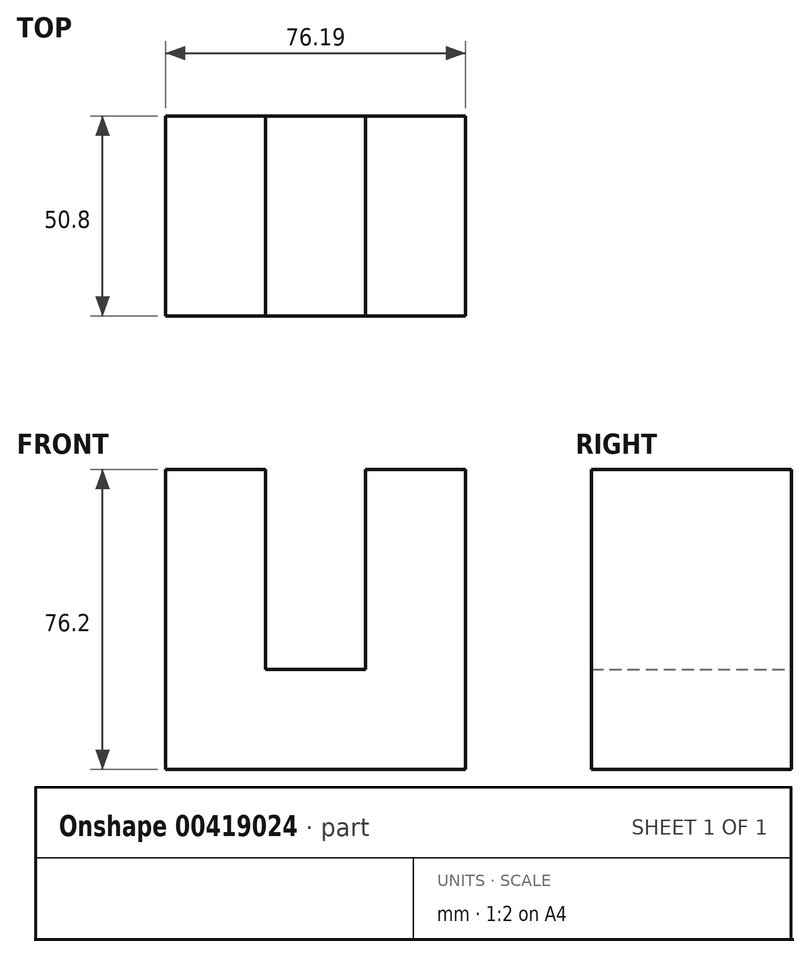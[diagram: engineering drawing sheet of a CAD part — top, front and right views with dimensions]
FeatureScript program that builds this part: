
annotation { "Feature Type Name" : "Feature", "Feature Type Description" : "" }
export const myFeature = defineFeature(function(context is Context, id is Id, definition is map)
    precondition{}
    {
        {
            var Q0;
            Q0=qCreatedBy(makeId("Front.planeOp"),FACE);
            var sketch = newSketch(context, id + "F0", { "sketchPlane" : qUnion([Q0])});
            skLineSegment(sketch, "E0", {"start": v(0, 0) * mm, "end": v(-76.2, 0) * mm});
            skLineSegment(sketch, "E1", {"start": v(-76.2, 0) * mm, "end": v(-76.2, 76.2) * mm});
            skLineSegment(sketch, "E2", {"start": v(-76.2, 76.2) * mm, "end": v(-50.78, 76.2) * mm});
            skLineSegment(sketch, "E3", {"start": v(-50.78, 76.2) * mm, "end": v(-50.78, 25.4) * mm});
            skLineSegment(sketch, "E4", {"start": v(0, 0) * mm, "end": v(0, 76.2) * mm});
            skLineSegment(sketch, "E5", {"start": v(0, 76.2) * mm, "end": v(-25.4, 76.2) * mm});
            skLineSegment(sketch, "E6", {"start": v(-25.4, 76.2) * mm, "end": v(-25.4, 25.4) * mm});
            skLineSegment(sketch, "E7", {"start": v(-25.4, 25.4) * mm, "end": v(-50.78, 25.4) * mm});
            skSolve(sketch);
        }
        {
            var Q0;
            Q0=makeQuery(id+"F0.imprint","IMPRINT",FACE,{"disambiguationData":[TD([[makeQuery(id+"F0.imprint","IMPRINT",EDGE,{"derivedFrom":sQuery(id+"F0.wireOp",EDGE,"E0")}),-1.0]])]});
            extrude(context, id + "F1", {"entities" : qUnion([Q0]), "depth" : 50.8 * mm});
        }
    });
